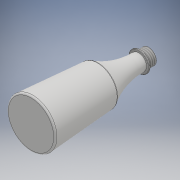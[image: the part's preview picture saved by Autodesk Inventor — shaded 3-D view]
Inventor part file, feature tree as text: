
AUTODESK INVENTOR PART (.ipt)
format: ipt  version: 2018 (Build 220112000, 112)  size: 216,576 bytes
history: native  units: mm
features: fillet x3, revolve x1, shell x1, thread x1, sketch x1
ambient origin geometry x8: Origin, YZ Plane, XZ Plane, XY Plane, X Axis, Y Axis, Z Axis, Center Point
bodies: Solid1 (feature_tree)
feature tree (7):
  revolve  "Revolution1"  [1 undecoded]
  shell  "Shell1"  Thickness=2.0mm
  fillet  "Fillet1"  Radius=2.0mm
  fillet  "Fillet2"  Radius=0.5mm
  fillet  "Fillet3"  Radius=10.0mm
  thread  "Thread1"  [1 undecoded]
  sketch  "Sketch1"  dims[d1=90.0deg d2=1.0mm d3=2.0mm d4=2.0mm d5=0.5mm d6=10.0mm d7=0.0mm]
note: 2 required parameter values undecoded (feature->parameter linkage not recoverable at this tier; creation-order binding heuristic only, values carry confidence <= 0.55)